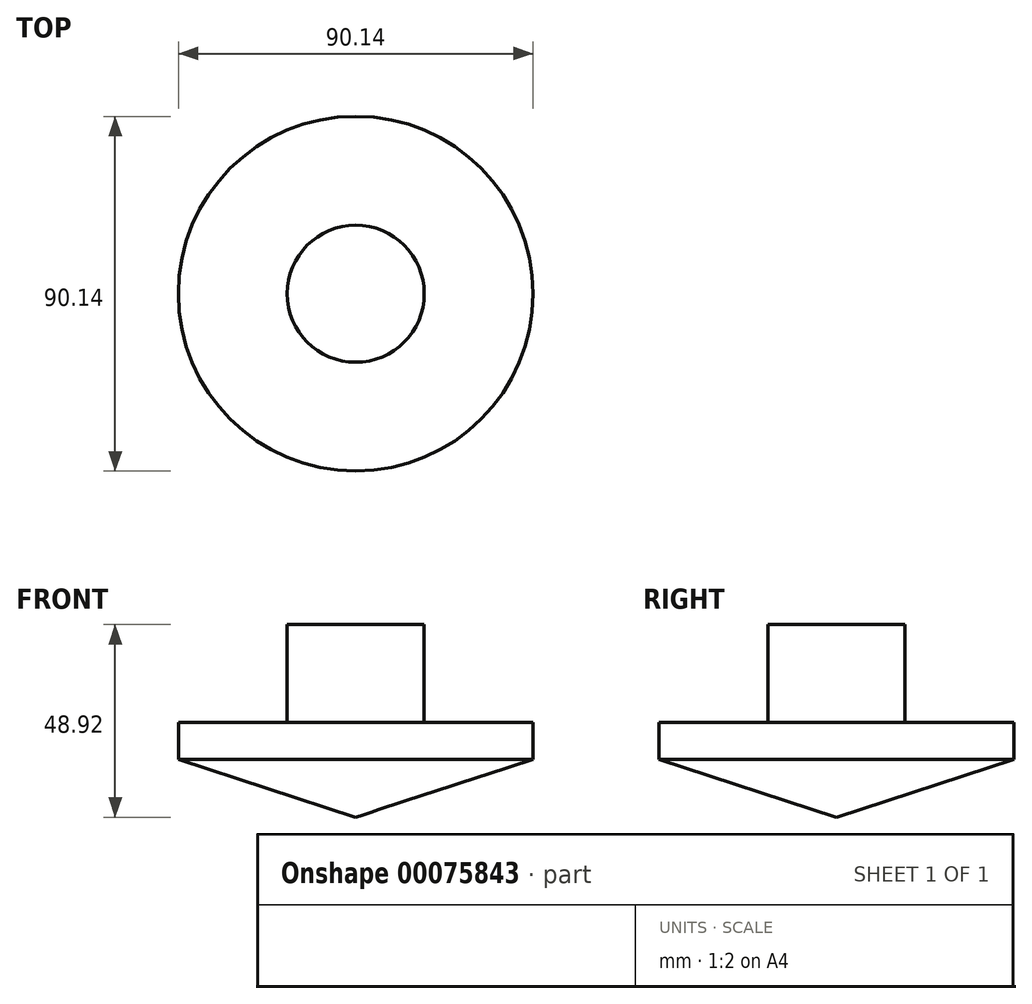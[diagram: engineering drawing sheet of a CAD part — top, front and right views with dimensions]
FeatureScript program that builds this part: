
annotation { "Feature Type Name" : "Feature", "Feature Type Description" : "" }
export const myFeature = defineFeature(function(context is Context, id is Id, definition is map)
    precondition{}
    {
        {
            var Q0;
            Q0=qCreatedBy(makeId("Front.planeOp"),FACE);
            var sketch = newSketch(context, id + "F0", { "sketchPlane" : qUnion([Q0])});
            skLineSegment(sketch, "E0", {"start": v(0, 0) * mm, "end": v(50.2, 21.54) * mm});
            skLineSegment(sketch, "E1", {"start": v(50.2, 21.54) * mm, "end": v(50.2, 36.37) * mm});
            skLineSegment(sketch, "E2", {"start": v(50.2, 36.37) * mm, "end": v(20.54, 36.37) * mm});
            skLineSegment(sketch, "E3", {"start": v(20.54, 36.37) * mm, "end": v(20.54, 50.06) * mm});
            skLineSegment(sketch, "E4", {"start": v(20.54, 50.06) * mm, "end": v(0, 50.06) * mm});
            skLineSegment(sketch, "E5", {"start": v(0, 50.06) * mm, "end": v(0, 0) * mm});
            skSolve(sketch);
        }
        {
            var Q0;
            Q0=qCreatedBy(makeId("Front.planeOp"),FACE);
            var sketch = newSketch(context, id + "F1", { "sketchPlane" : qUnion([Q0])});
            skLineSegment(sketch, "E6", {"start": v(0, 0) * mm, "end": v(45.07, 14.69) * mm});
            skLineSegment(sketch, "E7", {"start": v(45.07, 14.69) * mm, "end": v(45.07, 24.1) * mm});
            skLineSegment(sketch, "E8", {"start": v(17.4, 24.1) * mm, "end": v(45.07, 24.1) * mm});
            skLineSegment(sketch, "E9", {"start": v(17.4, 24.1) * mm, "end": v(17.4, 48.92) * mm});
            skLineSegment(sketch, "E10", {"start": v(17.4, 48.92) * mm, "end": v(0, 48.92) * mm});
            skLineSegment(sketch, "E11", {"start": v(0, 48.92) * mm, "end": v(0, 0) * mm});
            skSolve(sketch);
        }
        {
            var Q0;
            Q0=makeQuery(id+"F1.imprint","IMPRINT",FACE,{"disambiguationData":[TD([[makeQuery(id+"F1.imprint","IMPRINT",EDGE,{"derivedFrom":sQuery(id+"F1.wireOp",EDGE,"E6")}),1.0]])]});
            var Q1;
            Q1=sQuery(id+"F1.wireOp",EDGE,"E11");
            revolve(context, id + "F2", {"entities" : qUnion([Q0]), "axis" : qUnion([Q1]), "revolveType" : RevolveType.FULL});
        }
    });
